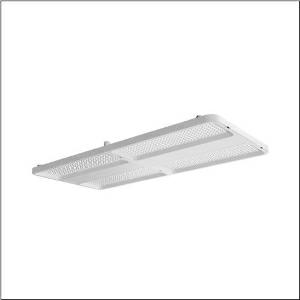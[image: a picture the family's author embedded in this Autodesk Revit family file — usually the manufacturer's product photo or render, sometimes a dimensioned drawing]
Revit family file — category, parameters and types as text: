
# Revit family: highbay_11_maxi_51hn11db4rda
name_source: partatom
category: Lighting Fixtures
units: mm (PartAtom-declared; Revit-internal decimal feet)

## family parameters
Cut with Voids When Loaded = No
Host = Face
Light Source = No
Part Type = Normal
Room Calculation Point = No
Round Connector Dimension = Use Diameter
Shared = No

## types (1)
- --- (1 x LED, 6720 lm, 32.8 W, 4000K)
    Apparent Load = 33 VA
    CIE Flux Codes = 85 97 100 100 100
    Color Rendering = 80
    Color Temperature = 4000K
    Default Elevation = 1800 mm
    Description = high bay luminaire Highbay 11 maxi; direct symmetric narrow distribution, light control with lens of PMMA; UGR ≤ 22 (X = 4H | Y = 8H | S = 0.25H | reflection values 70/50/20); luminous flux: 42.500lm; light colour: 840, colour temperature: 4000K, MacAdam ≤ 2 SDCM (initial), colour rendering: CRI > 80; luminous efficacy: 198,9lm/W; rated service life: 100.000h (L95/B50) at AT= 25°C; control: DALI 2; housing frame of high-performance plastic PA6, matt traffic white (RAL 9016); cover of PMMA; dimension (LxWxH): 946 x 442 x 72mm; luminaire connection: terminal, 5-pole, max. 2.5mm² (cable entry for one cable, Ø 8.5..16mm); mains connection: 230..240V, AC/DC 0/50..60Hz; connected load: 213,7W; protection rating (complete): IP66; insulation class (complete): insulation class I (protective earthing); protection symbol: D; impact resistance: IK08; halogen-free wiring; for central battery installations according to DIN EN 60598-2-22; corresponds to IFS (International Featured Standards) requirements for safety and quality in the food industry; LABS conformity tested according to VDMA 24364:2018-05; certification: CE, ENEC, VDE, UKCA; permissible operating ambient temperature: -40..+50°C (reducing of maximum allowable ambient temperature of 5°C with ceiling mounting); packaging unit: 1 piece; (delivery without accessories; please order mounting accessories separately)
    Height = 72 mm  [stored 0.23622 ft]
    Lamp = 1 x LED
    Lamp Light Flux = 6720 lm
    Lamp Power = 32.8 W
    Lamp count = 1
    Length = 946 mm
    Luminous efficacy = 205 lm/W
    Manufacturer = Siteco
    ModVariant = No
    Model = 51HN11DB4RDA
    Mounting Place = Ceiling
    Mounting Type = Pendant
    Number of Poles = 1
    OnlyDefault = Yes
    Power Factor = 1
    Product Name = Highbay 11 maxi
    Product group = high bay luminaire
    ProductGroupID = 901
    Protection Class = Protection class I
    Protection Degree = IP 66
    RLX_Detail_Level = 1
    RLX_Emergency_Light_Flux = 0 lm
    RLX_Emergency_Type = 0
    RLX_Emergency_Type_DB = No
    RlxData = <blob elided: 22345 chars, md5=19e11e15>
    Socket = socket
    Standby Power = 0 W
    System Light Flux = 6720 lm
    System Power = 33 W
    Type Comments = : DC mode (central or group accumulator) initial emergency light level
    Type Image = l_1363244.jpg
    URL = http://relux.com
    VarID = @adj_003703
    Voltage = 0 V
    Weight = 0.00 kg
    Width = 442 mm

note: [stored X ft] marks values corroborated as IEEE doubles in the binary element streams (Revit-internal decimal feet)

## geometry (parser evidence)
native form markers: Blend x4, Sweep x9
no freeform markers — native parametric forms only
